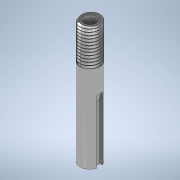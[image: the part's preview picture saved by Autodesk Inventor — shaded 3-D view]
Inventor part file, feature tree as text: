
AUTODESK INVENTOR PART (.ipt)
format: ipt  version: 2020 (Build 240168000, 168)  size: 952,832 bytes
history: native  units: in
note: dims shown in document units (in); Inventor stores cm internally (conversion verified against a paired STEP export)
features: sketch x6, extrude x3, revolve x2, thread x1, fillet x1, helix x1
ambient origin geometry x8: Origin, YZ Plane, XZ Plane, XY Plane, X Axis, Y Axis, Z Axis, Center Point
bodies: Solid1 (feature_tree), Solid2 (feature_tree)
feature tree (14):
  extrude  "Extrusion1"  Depth=3.875in TaperAngle=0.0deg
  extrude  "Extrusion2"  Depth=2.0in TaperAngle=0.0deg
  thread  "Thread1"  [1 undecoded]
  extrude  "Extrusion3"  Depth=0.0938in
  fillet  "Fillet1"  Radius=2.0in
  revolve  "Revolution1"  [1 undecoded]
  revolve  "Revolution2"  [1 undecoded]
  helix  "Coil1"  [1 undecoded]
  sketch  "Sketch1"  dims[d0=0.624in d1=3.875in d2=0.0in]
  sketch  "Sketch2"  dims[d3=0.374in d4=2.0in d5=0.0in d6=1.125in d7=0.0in]
  sketch  "Sketch3"  dims[d8=0.0938in d9=0.0938in d10=2.0in d11=0.0in]
  sketch  "Sketch4"  dims[d12=0.4375in d13=0.3779in d14=0.0146in d15=0.0146in]
  sketch  "Sketch5"  dims[d18=0.0909in d20=0.3779in d22=0.0in]
  sketch  "Sketch6"  dims[d23=0.0in d24=0.091in d25=1.3068in d26=0.3937in d27=0.0in d28=0.0in d29=0.0in d30=0.0in d31=0.0in]
note: 4 required parameter values undecoded (feature->parameter linkage not recoverable at this tier; creation-order binding heuristic only, values carry confidence <= 0.55)